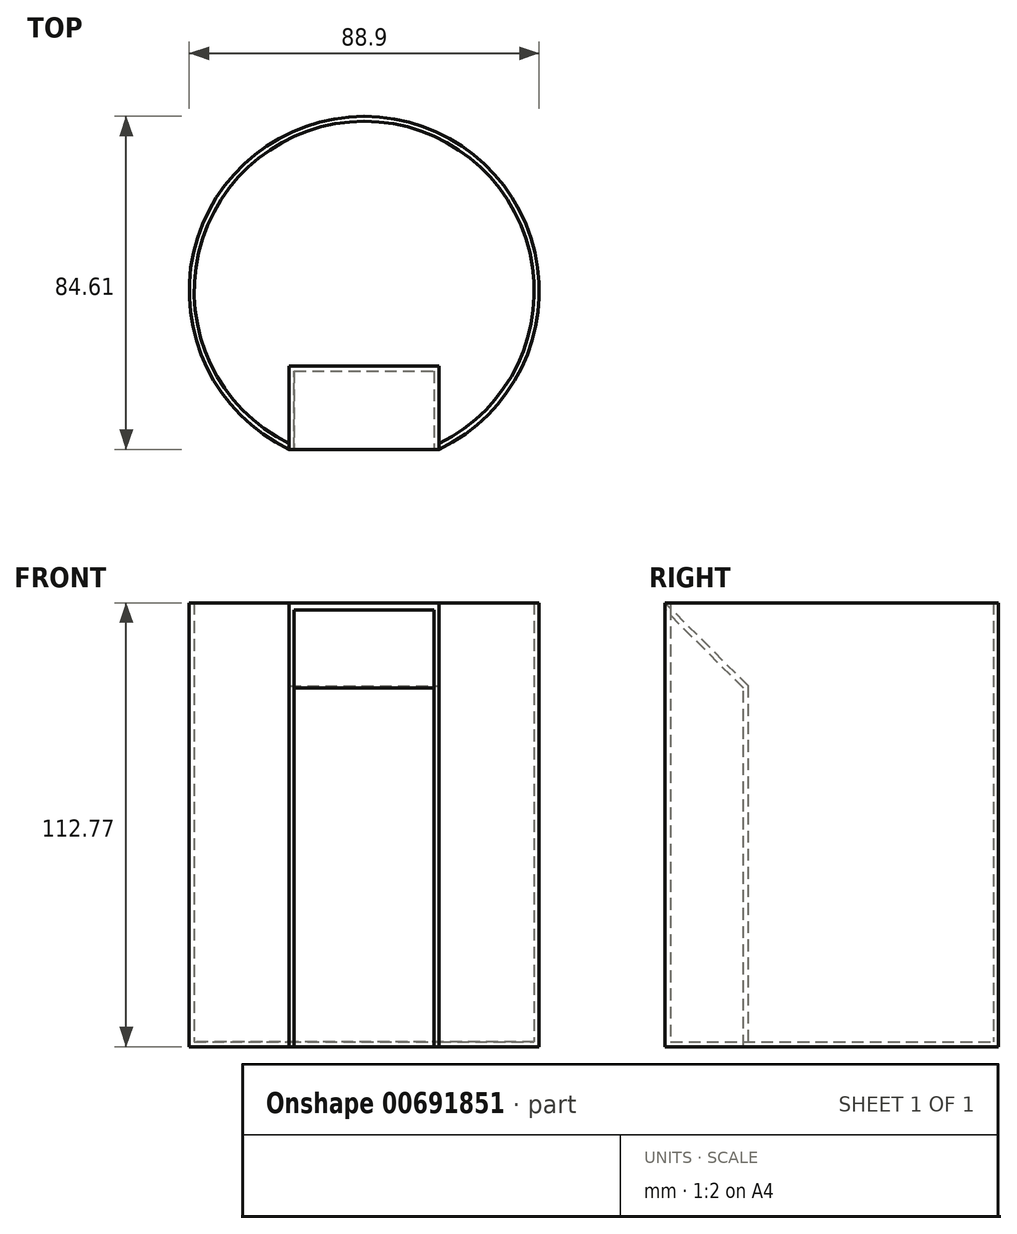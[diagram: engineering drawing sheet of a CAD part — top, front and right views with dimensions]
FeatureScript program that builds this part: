
annotation { "Feature Type Name" : "Feature", "Feature Type Description" : "" }
export const myFeature = defineFeature(function(context is Context, id is Id, definition is map)
    precondition{}
    {
        {
            var Q0;
            Q0=qCreatedBy(makeId("Top.planeOp"),FACE);
            var sketch = newSketch(context, id + "F0", { "sketchPlane" : qUnion([Q0])});
            skArc(sketch, "E0", {"start": v(19.05, -40.16) * mm, "mid": v(0, 44.45) * mm, "end": v(-19.05, -40.16) * mm});
            skLineSegment(sketch, "E1.top", {"start": v(-19.05, -19.05) * mm, "end": v(19.05, -19.05) * mm});
            skLineSegment(sketch, "E1.left", {"start": v(-19.05, -40.16) * mm, "end": v(-19.05, -19.05) * mm});
            skLineSegment(sketch, "E1.right", {"start": v(19.05, -40.16) * mm, "end": v(19.05, -19.05) * mm});
            skPoint(sketch, "E2", {"position": v(0, -44.45) * mm});
            skLineSegment(sketch, "E3", {"start": v(0, -44.45) * mm, "end": v(0, 0) * mm});
            skArc(sketch, "E4", {"start": v(19.05, -38.75) * mm, "mid": v(0, 43.18) * mm, "end": v(-19.05, -38.75) * mm});
            skSolve(sketch);
        }
        {
            var Q0;
            Q0=qCreatedBy(makeId("Right.planeOp"),FACE);
            var Q1;
            Q1=sQuery(id+"F0.wireOp",VERTEX,"E0.start");
            cPlane(context, id + "F1", {"entities" : qUnion([Q0, Q1]), "cplaneType" : CPlaneType.PLANE_POINT, "offset" : 25.4 * mm, "width" : 152.4 * mm, "height" : 152.4 * mm});
        }
        {
            var Q0;
            Q0=qCreatedBy(id+"F1.planeOp",FACE);
            var sketch = newSketch(context, id + "F2", { "sketchPlane" : qUnion([Q0])});
            skLineSegment(sketch, "E5.bottom", {"start": v(-19.05, 0) * mm, "end": v(-20.32, 0) * mm});
            skLineSegment(sketch, "E5.left", {"start": v(-19.05, 0) * mm, "end": v(-19.05, 91.66) * mm});
            skLineSegment(sketch, "E6", {"start": v(-19.05, 91.66) * mm, "end": v(-40.16, 112.77) * mm});
            skLineSegment(sketch, "E7.1", {"start": v(-20.32, 91.14) * mm, "end": v(-38.9, 109.7) * mm});
            skLineSegment(sketch, "E7.4", {"start": v(-20.32, 1.27) * mm, "end": v(-20.32, 91.14) * mm});
            skLineSegment(sketch, "E8", {"start": v(-38.9, 109.7) * mm, "end": v(-40.16, 110.97) * mm});
            skLineSegment(sketch, "E9", {"start": v(-40.16, 110.97) * mm, "end": v(-40.16, 112.77) * mm});
            skLineSegment(sketch, "E10", {"start": v(-20.32, 1.27) * mm, "end": v(-20.32, 0) * mm});
            skLineSegment(sketch, "E11", {"start": v(-40.16, 110.97) * mm, "end": v(-40.16, 0) * mm});
            skLineSegment(sketch, "E12", {"start": v(-40.16, 0) * mm, "end": v(-20.32, 0) * mm});
            skSolve(sketch);
        }
        {
            var Q0;
            Q0=makeQuery(id+"F2.imprint","IMPRINT",FACE,{"disambiguationData":[TD([[makeQuery(id+"F2.imprint","IMPRINT",EDGE,{"derivedFrom":sQuery(id+"F2.wireOp",EDGE,"E7.1")}),1.0]])]});
            extrude(context, id + "F3", {"entities" : qUnion([Q0]), "oppositeDirection" : true, "depth" : 1.27 * mm, "offsetDistance" : 25.4 * mm});
        }
        {
            var Q0;
            Q0=makeQuery(id+"F2.imprint","IMPRINT",FACE,{"disambiguationData":[TD([[makeQuery(id+"F2.imprint","IMPRINT",EDGE,{"derivedFrom":sQuery(id+"F2.wireOp",EDGE,"E5.bottom")}),-1.0]])]});
            extrude(context, id + "F4", {"entities" : qUnion([Q0]), "operationType" : NewBodyOperationType.ADD, "oppositeDirection" : true, "depth" : 38.1 * mm, "offsetDistance" : 25.4 * mm});
        }
        {
            var Q0;
            Q0=makeQuery(id+"F4.opExtrude","CAP_FACE",FACE,{"disambiguationData":[OSD([sQuery(id+"F2.wireOp",EDGE,"E5.bottom"),sQuery(id+"F2.wireOp",EDGE,"E5.left"),sQuery(id+"F2.wireOp",EDGE,"E6"),sQuery(id+"F2.wireOp",EDGE,"E7.1"),sQuery(id+"F2.wireOp",EDGE,"E7.4"),sQuery(id+"F2.wireOp",EDGE,"E8"),sQuery(id+"F2.wireOp",EDGE,"E9"),sQuery(id+"F2.wireOp",EDGE,"E10")])],"isStart":false});
            cPlane(context, id + "F5", {"entities" : qUnion([Q0]), "cplaneType" : CPlaneType.OFFSET, "offset" : 0 * mm, "width" : 152.4 * mm, "height" : 152.4 * mm});
        }
        {
            var Q0;
            Q0=qCreatedBy(id+"F5.planeOp",FACE);
            var sketch = newSketch(context, id + "F6", { "sketchPlane" : qUnion([Q0])});
            skLineSegment(sketch, "E13", {"start": v(40.16, 0) * mm, "end": v(20.32, 0) * mm});
            skLineSegment(sketch, "E14", {"start": v(20.32, 0) * mm, "end": v(20.32, 91.14) * mm});
            skLineSegment(sketch, "E15", {"start": v(20.32, 91.14) * mm, "end": v(40.16, 110.97) * mm});
            skLineSegment(sketch, "E16", {"start": v(40.16, 110.97) * mm, "end": v(40.16, 0) * mm});
            skSolve(sketch);
        }
        {
            var Q0;
            Q0=makeQuery(id+"F6.imprint","IMPRINT",FACE,{"disambiguationData":[TD([[makeQuery(id+"F6.imprint","IMPRINT",EDGE,{"derivedFrom":sQuery(id+"F6.wireOp",EDGE,"E13")}),-1.0]])]});
            extrude(context, id + "F7", {"entities" : qUnion([Q0]), "operationType" : NewBodyOperationType.ADD, "oppositeDirection" : true, "depth" : 1.27 * mm, "offsetDistance" : 25.4 * mm});
        }
        {
            var Q0;
            {var subQ0=sQuery(id+"F0.wireOp",EDGE,"E0");Q0=makeQuery(id+"F0.imprint","IMPRINT",FACE,{"disambiguationData":[TD([[makeQuery(id+"F0.imprint","IMPRINT",EDGE,{"derivedFrom":subQ0}),1.0]])]});}
            var Q1;
            Q1=makeQuery(id+"F4.opExtrude","CAP_VERTEX",VERTEX,{"disambiguationData":[OSD([sQuery(id+"F2.wireOp",EDGE,"E6"),sQuery(id+"F2.wireOp",EDGE,"E9")])],"isStart":true});
            extrude(context, id + "F8", {"entities" : qUnion([Q0]), "operationType" : NewBodyOperationType.ADD, "endBound" : BoundingType.UP_TO_VERTEX, "depth" : 25.4 * mm, "endBoundEntityVertex" : qUnion([Q1]), "offsetDistance" : 25.4 * mm});
        }
        {
            var Q0;
            {var subQ5=sQuery(id+"F0.wireOp",EDGE,"E4");Q0=makeQuery(id+"F0.imprint","IMPRINT",FACE,{"disambiguationData":[TD([[makeQuery(id+"F0.imprint","IMPRINT",EDGE,{"derivedFrom":subQ5}),1.0]])]});}
            extrude(context, id + "F9", {"entities" : qUnion([Q0]), "operationType" : NewBodyOperationType.ADD, "depth" : 1.27 * mm, "offsetDistance" : 25.4 * mm});
        }
    });
